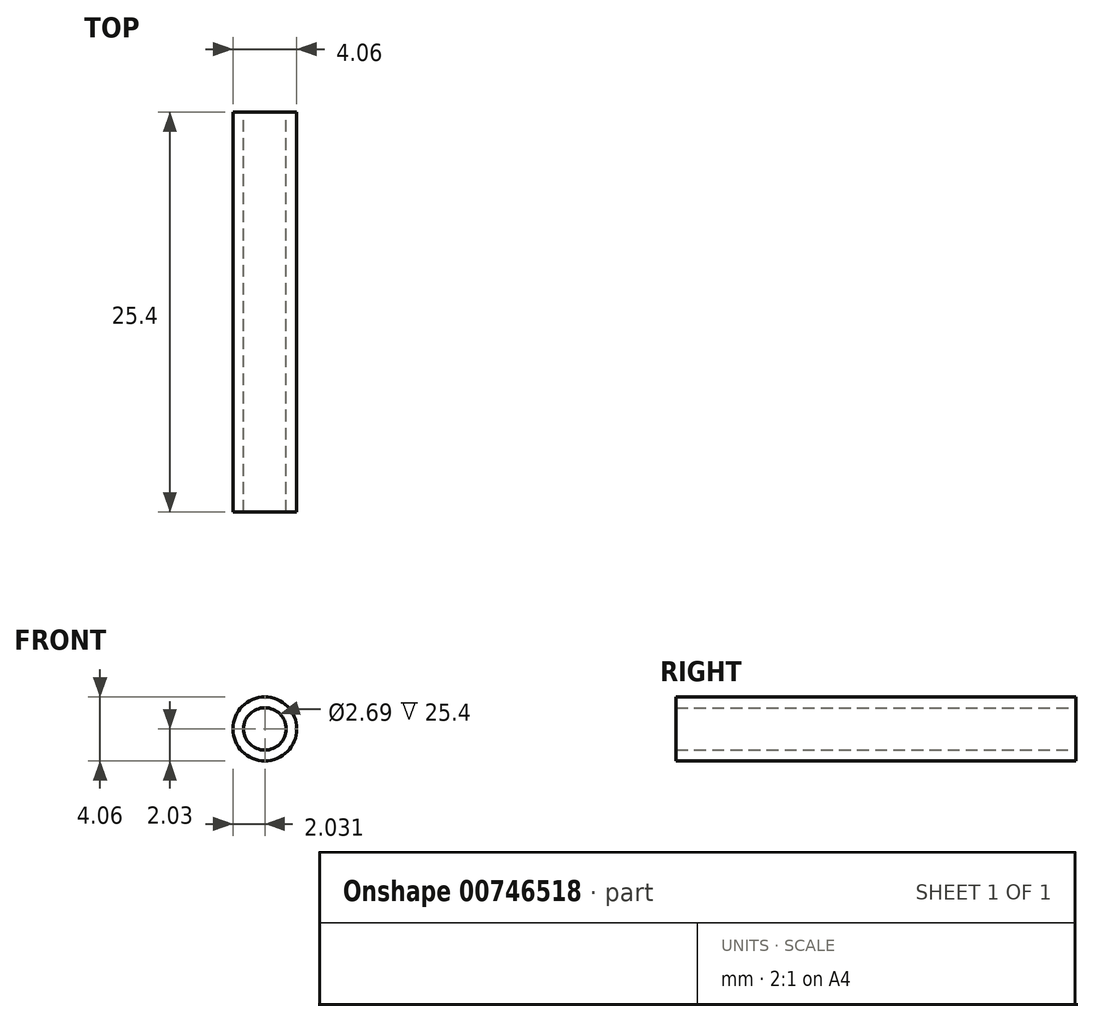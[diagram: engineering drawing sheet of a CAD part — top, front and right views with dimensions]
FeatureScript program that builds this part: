
annotation { "Feature Type Name" : "Feature", "Feature Type Description" : "" }
export const myFeature = defineFeature(function(context is Context, id is Id, definition is map)
    precondition{}
    {
        {
            var Q0;
            Q0=qCreatedBy(makeId("Front.planeOp"),FACE);
            var sketch = newSketch(context, id + "F0", { "sketchPlane" : qUnion([Q0])});
            skCircle(sketch, "E0", {"center": v(-4.83, -1.15) * mm, "radius": 2.03 * mm});
            skSolve(sketch);
        }
        {
            var Q0;
            Q0=makeQuery(id+"F0.imprint","IMPRINT",FACE,{"disambiguationData":[TD([[makeQuery(id+"F0.imprint","IMPRINT",EDGE,{"derivedFrom":sQuery(id+"F0.wireOp",EDGE,"E0")}),1.0]])]});
            extrude(context, id + "F1", {"entities" : qUnion([Q0]), "depth" : 25.4 * mm, "offsetDistance" : 25.4 * mm});
        }
        {
            var Q0;
            Q0=makeQuery(id+"F1.opExtrude","CAP_FACE",FACE,{"disambiguationData":[OSD([sQuery(id+"F0.wireOp",EDGE,"E0")])],"isStart":true});
            var sketch = newSketch(context, id + "F2", { "sketchPlane" : qUnion([Q0])});
            skCircle(sketch, "E1", {"center": v(4.83, -1.15) * mm, "radius": 1.35 * mm});
            skSolve(sketch);
        }
        {
            var Q0;
            Q0=makeQuery(id+"F2.imprint","IMPRINT",FACE,{"disambiguationData":[TD([[makeQuery(id+"F2.imprint","IMPRINT",EDGE,{"derivedFrom":sQuery(id+"F2.wireOp",EDGE,"MvJZRzMe-IXuE-yWny-WodI-AlLfAxLdQXFD")}),1.0]])]});
            var Q1;
            Q1=makeQuery(id+"F2.imprint","IMPRINT",FACE,{"disambiguationData":[TD([[makeQuery(id+"F2.imprint","IMPRINT",EDGE,{"derivedFrom":sQuery(id+"F2.wireOp",EDGE,"E1")}),1.0]])]});
            extrude(context, id + "F3", {"entities" : qUnion([Q0, Q1]), "operationType" : NewBodyOperationType.REMOVE, "oppositeDirection" : true, "depth" : 25.4 * mm, "offsetDistance" : 25.4 * mm});
        }
    });
